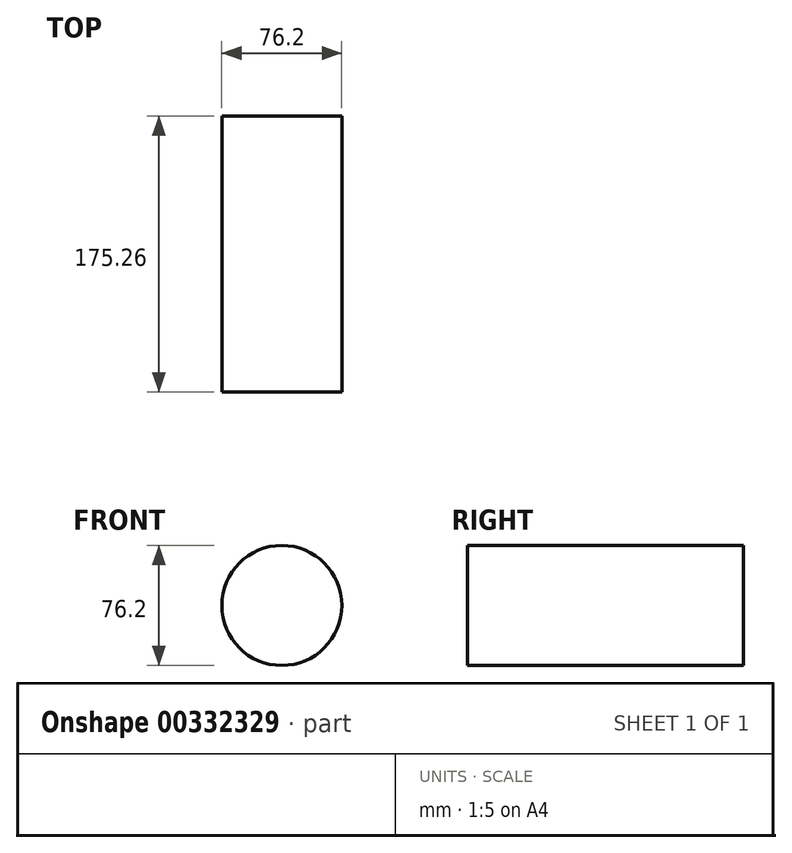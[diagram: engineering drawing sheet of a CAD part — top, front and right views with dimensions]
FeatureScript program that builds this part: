
annotation { "Feature Type Name" : "Feature", "Feature Type Description" : "" }
export const myFeature = defineFeature(function(context is Context, id is Id, definition is map)
    precondition{}
    {
        {
            var Q0;
            Q0=qCreatedBy(makeId("Front.planeOp"),FACE);
            var sketch = newSketch(context, id + "F0", { "sketchPlane" : qUnion([Q0])});
            skCircle(sketch, "E0", {"center": v(-112.05, 60.55) * mm, "radius": 38.1 * mm});
            skSolve(sketch);
        }
        {
            var Q0;
            Q0=makeQuery(id+"F0.imprint","IMPRINT",FACE,{"disambiguationData":[TD([[makeQuery(id+"F0.imprint","IMPRINT",EDGE,{"derivedFrom":sQuery(id+"F0.wireOp",EDGE,"E0")}),1.0]])]});
            extrude(context, id + "F1", {"entities" : qUnion([Q0]), "depth" : 175.26 * mm});
        }
    });
